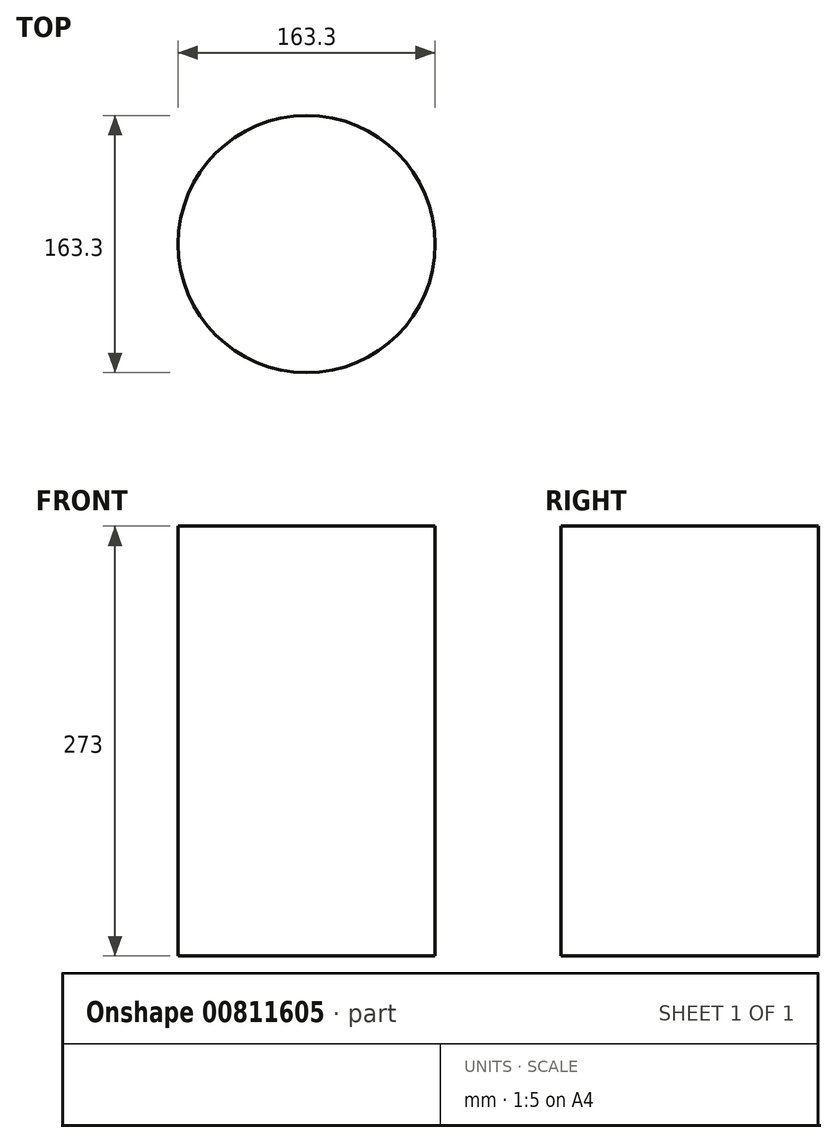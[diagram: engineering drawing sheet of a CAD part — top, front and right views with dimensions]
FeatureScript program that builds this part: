
annotation { "Feature Type Name" : "Feature", "Feature Type Description" : "" }
export const myFeature = defineFeature(function(context is Context, id is Id, definition is map)
    precondition{}
    {
        {
            var Q0;
            Q0=qCreatedBy(makeId("Top.planeOp"),FACE);
            var sketch = newSketch(context, id + "F0", { "sketchPlane" : qUnion([Q0])});
            skCircle(sketch, "E0", {"center": v(0, 0) * mm, "radius": 81.65 * mm});
            skSolve(sketch);
        }
        {
            var Q0;
            Q0 = qSketchRegion(id + "F0", true);
            extrude(context, id + "F1", {"entities" : qUnion([Q0]), "depth" : 273 * mm, "offsetDistance" : 25 * mm});
        }
    });
